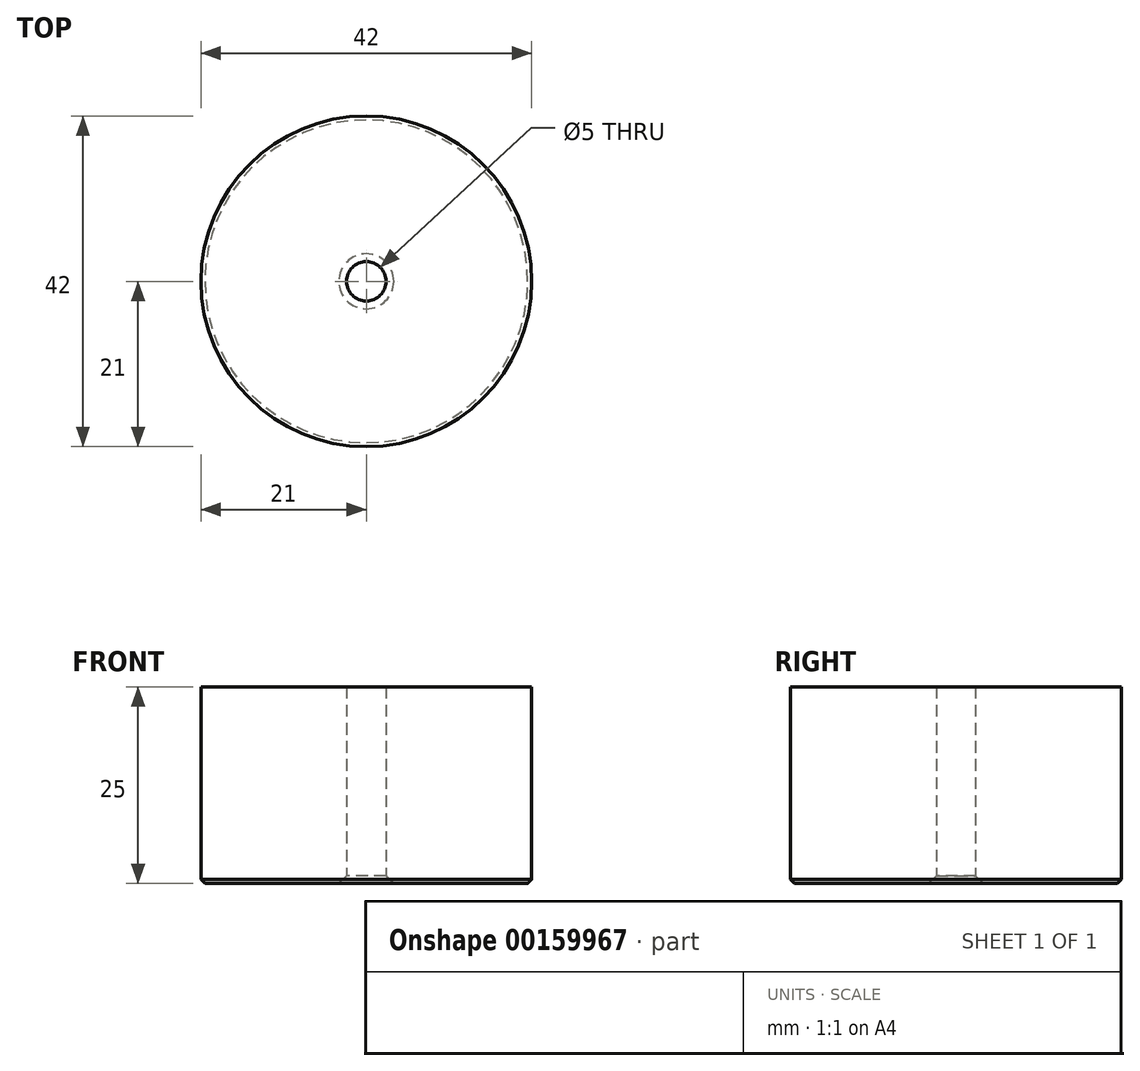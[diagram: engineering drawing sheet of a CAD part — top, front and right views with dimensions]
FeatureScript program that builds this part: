
annotation { "Feature Type Name" : "Feature", "Feature Type Description" : "" }
export const myFeature = defineFeature(function(context is Context, id is Id, definition is map)
    precondition{}
    {
        {
            var Q0;
            Q0=qCreatedBy(makeId("Top.planeOp"),FACE);
            var sketch = newSketch(context, id + "F0", { "sketchPlane" : qUnion([Q0])});
            skCircle(sketch, "E0", {"center": v(0, 0) * mm, "radius": 21 * mm});
            skCircle(sketch, "E1", {"center": v(0, 0) * mm, "radius": 2.5 * mm});
            skSolve(sketch);
        }
        {
            var Q0;
            Q0 = qSketchRegion(id + "F0", true);
            extrude(context, id + "F1", {"entities" : qUnion([Q0]), "depth" : 25 * mm});
        }
        {
            var Q0;
            Q0=makeQuery(id+"F1.opExtrude","CAP_EDGE",EDGE,{"disambiguationData":[OSD([sQuery(id+"F0.wireOp",EDGE,"E1")])],"isStart":true});
            chamfer(context, id + "F2", {"entities" : qUnion([Q0]), "width" : 1 * mm, "tangentPropagation" : true});
        }
        {
            var Q0;
            Q0=makeQuery(id+"F1.opExtrude","CAP_EDGE",EDGE,{"disambiguationData":[OSD([sQuery(id+"F0.wireOp",EDGE,"E0")])],"isStart":true});
            chamfer(context, id + "F3", {"entities" : qUnion([Q0]), "width" : 0.5 * mm, "tangentPropagation" : true});
        }
    });
